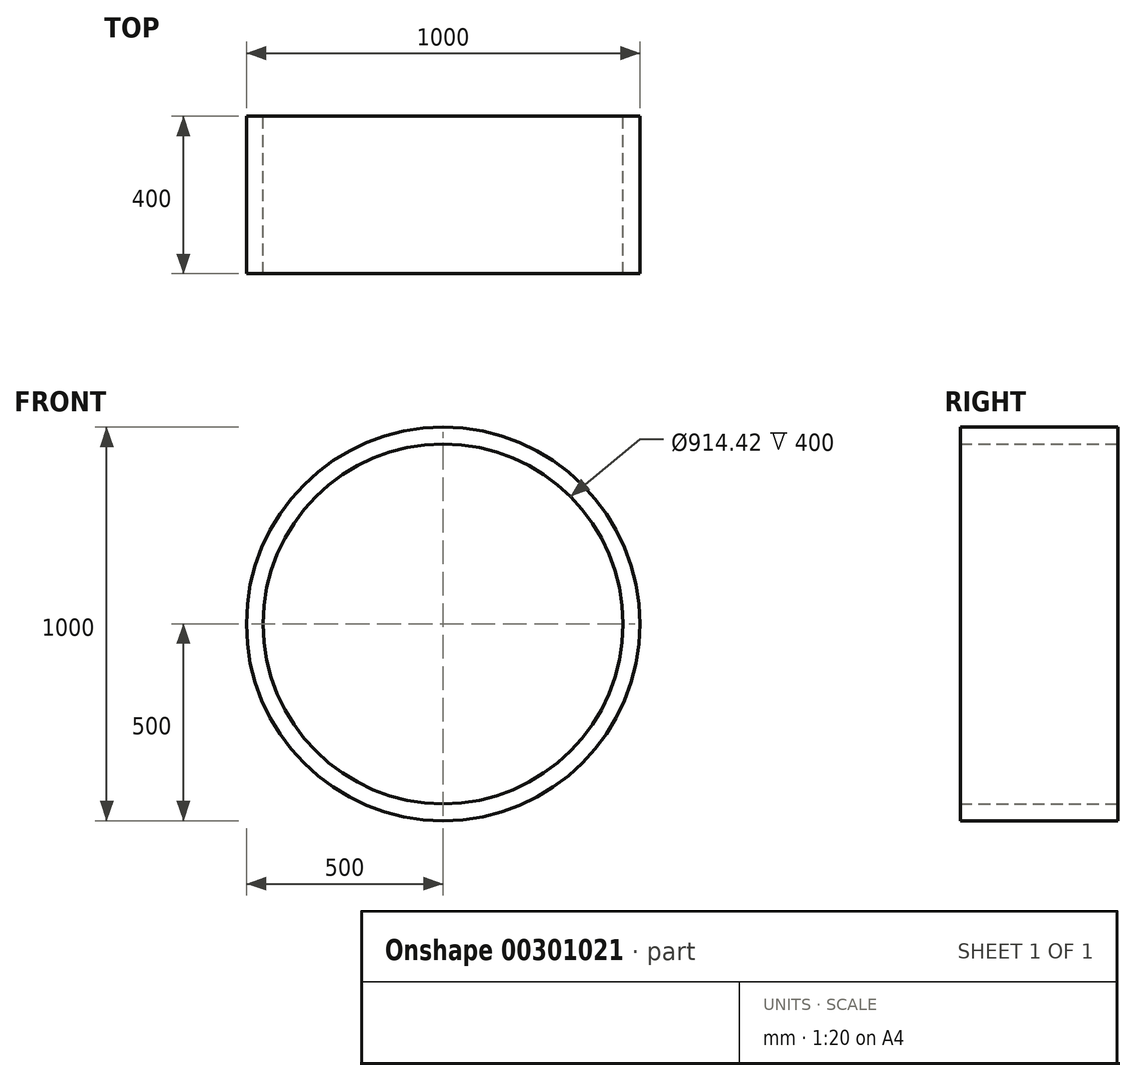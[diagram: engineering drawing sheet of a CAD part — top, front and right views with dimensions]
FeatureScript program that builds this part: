
annotation { "Feature Type Name" : "Feature", "Feature Type Description" : "" }
export const myFeature = defineFeature(function(context is Context, id is Id, definition is map)
    precondition{}
    {
        {
            var Q0;
            Q0=qCreatedBy(makeId("Front.planeOp"),FACE);
            var sketch = newSketch(context, id + "F0", { "sketchPlane" : qUnion([Q0])});
            skCircle(sketch, "E0", {"center": v(0, 0) * mm, "radius": 500 * mm});
            skCircle(sketch, "E1", {"center": v(0, 0) * mm, "radius": 457.2 * mm});
            skSolve(sketch);
        }
        {
            var Q0;
            Q0 = qSketchRegion(id + "F0", true);
            extrude(context, id + "F1", {"entities" : qUnion([Q0]), "depth" : 400 * mm});
        }
    });
